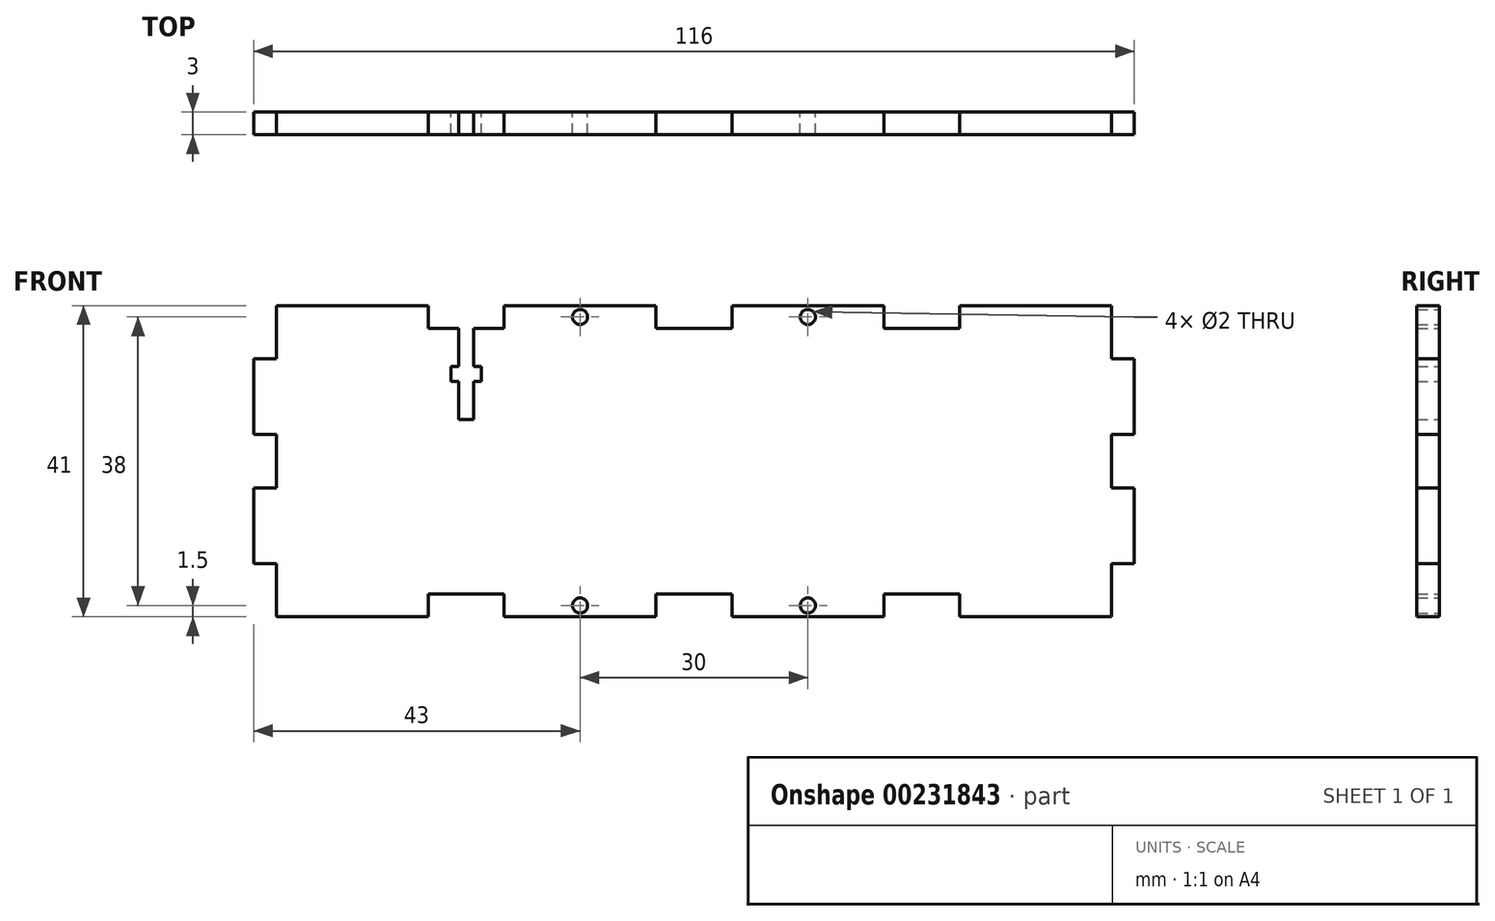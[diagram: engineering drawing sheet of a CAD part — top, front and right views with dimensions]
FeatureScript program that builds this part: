
annotation { "Feature Type Name" : "Feature", "Feature Type Description" : "" }
export const myFeature = defineFeature(function(context is Context, id is Id, definition is map)
    precondition{}
    {
        {
            var Q0;
            Q0=qCreatedBy(makeId("Front.planeOp"),FACE);
            var sketch = newSketch(context, id + "F0", { "sketchPlane" : qUnion([Q0])});
            skLineSegment(sketch, "E0", {"start": v(0, 0) * mm, "end": v(0, 7) * mm});
            skLineSegment(sketch, "E1", {"start": v(0, 7) * mm, "end": v(3, 7) * mm});
            skLineSegment(sketch, "E2", {"start": v(3, 7) * mm, "end": v(3, 17) * mm});
            skLineSegment(sketch, "E3", {"start": v(3, 17) * mm, "end": v(0, 17) * mm});
            skLineSegment(sketch, "E4", {"start": v(0, 17) * mm, "end": v(0, 24) * mm});
            skLineSegment(sketch, "E5", {"start": v(0, 24) * mm, "end": v(3, 24) * mm});
            skLineSegment(sketch, "E6", {"start": v(3, 24) * mm, "end": v(3, 34) * mm});
            skLineSegment(sketch, "E7", {"start": v(3, 34) * mm, "end": v(0, 34) * mm});
            skLineSegment(sketch, "E8", {"start": v(0, 34) * mm, "end": v(0, 41) * mm});
            skLineSegment(sketch, "E9", {"start": v(0, 41) * mm, "end": v(-20, 41) * mm});
            skLineSegment(sketch, "E10", {"start": v(-20, 41) * mm, "end": v(-20, 38) * mm});
            skLineSegment(sketch, "E11", {"start": v(-20, 38) * mm, "end": v(-30, 38) * mm});
            skLineSegment(sketch, "E12", {"start": v(-30, 38) * mm, "end": v(-30, 41) * mm});
            skLineSegment(sketch, "E13", {"start": v(-30, 41) * mm, "end": v(-50, 41) * mm});
            skLineSegment(sketch, "E14", {"start": v(-50, 41) * mm, "end": v(-50, 38) * mm});
            skLineSegment(sketch, "E15", {"start": v(-50, 38) * mm, "end": v(-60, 38) * mm});
            skLineSegment(sketch, "E16", {"start": v(-60, 38) * mm, "end": v(-60, 41) * mm});
            skLineSegment(sketch, "E17", {"start": v(-60, 41) * mm, "end": v(-80, 41) * mm});
            skLineSegment(sketch, "E18", {"start": v(-80, 41) * mm, "end": v(-80, 38) * mm});
            skLineSegment(sketch, "E19", {"start": v(-80, 38) * mm, "end": v(-84, 38) * mm});
            skLineSegment(sketch, "E20", {"start": v(-90, 38) * mm, "end": v(-90, 41) * mm});
            skLineSegment(sketch, "E21", {"start": v(-90, 41) * mm, "end": v(-110, 41) * mm});
            skLineSegment(sketch, "E22", {"start": v(0, 20.5) * mm, "end": v(-120, 20.5) * mm, "construction": true});
            skLineSegment(sketch, "E23.MirrorCS", {"start": v(-50, 0) * mm, "end": v(-50, 3) * mm});
            skLineSegment(sketch, "E24.MirrorCS", {"start": v(-60, 3) * mm, "end": v(-60, 0) * mm});
            skLineSegment(sketch, "E25.MirrorCS", {"start": v(-80, 0) * mm, "end": v(-80, 3) * mm});
            skLineSegment(sketch, "E26.MirrorCS", {"start": v(-90, 3) * mm, "end": v(-90, 0) * mm});
            skLineSegment(sketch, "E27.MirrorCS", {"start": v(-30, 3) * mm, "end": v(-30, 0) * mm});
            skLineSegment(sketch, "E28.MirrorCS", {"start": v(-20, 0) * mm, "end": v(-20, 3) * mm});
            skLineSegment(sketch, "E29.MirrorCS", {"start": v(-50, 3) * mm, "end": v(-60, 3) * mm});
            skLineSegment(sketch, "E30.MirrorCS", {"start": v(-60, 0) * mm, "end": v(-80, 0) * mm});
            skLineSegment(sketch, "E31.MirrorCS", {"start": v(-30, 0) * mm, "end": v(-50, 0) * mm});
            skLineSegment(sketch, "E32.MirrorCS", {"start": v(-80, 3) * mm, "end": v(-90, 3) * mm});
            skLineSegment(sketch, "E33.MirrorCS", {"start": v(-90, 0) * mm, "end": v(-110, 0) * mm});
            skLineSegment(sketch, "E34.MirrorCS", {"start": v(0, 0) * mm, "end": v(-20, 0) * mm});
            skLineSegment(sketch, "E35.MirrorCS", {"start": v(-20, 3) * mm, "end": v(-30, 3) * mm});
            skLineSegment(sketch, "E36", {"start": v(-55, 38) * mm, "end": v(-55, -6.16) * mm, "construction": true});
            skPoint(sketch, "E36.endSnap0", {"position": v(-55, 3) * mm});
            skLineSegment(sketch, "E37.MirrorCS", {"start": v(-113, 17) * mm, "end": v(-110, 17) * mm});
            skLineSegment(sketch, "E38.MirrorCS", {"start": v(-110, 24) * mm, "end": v(-113, 24) * mm});
            skLineSegment(sketch, "E39.MirrorCS", {"start": v(-113, 34) * mm, "end": v(-110, 34) * mm});
            skLineSegment(sketch, "E40.MirrorCS", {"start": v(-110, 7) * mm, "end": v(-113, 7) * mm});
            skLineSegment(sketch, "E41.MirrorCS", {"start": v(-110, 17) * mm, "end": v(-110, 24) * mm});
            skLineSegment(sketch, "E42.MirrorCS", {"start": v(-113, 7) * mm, "end": v(-113, 17) * mm});
            skLineSegment(sketch, "E43.MirrorCS", {"start": v(-113, 24) * mm, "end": v(-113, 34) * mm});
            skLineSegment(sketch, "E44.MirrorCS", {"start": v(-110, 34) * mm, "end": v(-110, 41) * mm});
            skLineSegment(sketch, "E45.MirrorCS", {"start": v(-110, 0) * mm, "end": v(-110, 7) * mm});
            skCircle(sketch, "E46", {"center": v(-40, 1.5) * mm, "radius": 1 * mm});
            skPoint(sketch, "E46.centerSnap0", {"position": v(-50, 1.5) * mm});
            skPoint(sketch, "E46.centerSnap1", {"position": v(-40, 0) * mm});
            skCircle(sketch, "E47.MirrorC", {"center": v(-70, 1.5) * mm, "radius": 1 * mm});
            skCircle(sketch, "E48.MirrorC", {"center": v(-70, 39.5) * mm, "radius": 1 * mm});
            skCircle(sketch, "E49.MirrorC", {"center": v(-40, 39.5) * mm, "radius": 1 * mm});
            skLineSegment(sketch, "E50", {"start": v(-85, 38) * mm, "end": v(-85, 18.99) * mm, "construction": true});
            skLineSegment(sketch, "E51.top", {"start": v(-86, 26) * mm, "end": v(-84, 26) * mm});
            skLineSegment(sketch, "E51.left", {"start": v(-86, 38) * mm, "end": v(-86, 33) * mm});
            skLineSegment(sketch, "E51.right", {"start": v(-84, 38) * mm, "end": v(-84, 33) * mm});
            skLineSegment(sketch, "E52.trimOffspring", {"start": v(-86, 38) * mm, "end": v(-90, 38) * mm});
            skLineSegment(sketch, "E53.bottom", {"start": v(-87, 33) * mm, "end": v(-86, 33) * mm});
            skLineSegment(sketch, "E53.top", {"start": v(-87, 31) * mm, "end": v(-86, 31) * mm});
            skLineSegment(sketch, "E53.left", {"start": v(-87, 33) * mm, "end": v(-87, 31) * mm});
            skLineSegment(sketch, "E53.right", {"start": v(-83, 33) * mm, "end": v(-83, 31) * mm});
            skLineSegment(sketch, "E54.trimOffspring", {"start": v(-84, 33) * mm, "end": v(-83, 33) * mm});
            skLineSegment(sketch, "E55.trimOffspring", {"start": v(-84, 31) * mm, "end": v(-84, 26) * mm});
            skLineSegment(sketch, "E56.trimOffspring", {"start": v(-86, 31) * mm, "end": v(-86, 26) * mm});
            skLineSegment(sketch, "E57.trimOffspring", {"start": v(-84, 31) * mm, "end": v(-83, 31) * mm});
            skSolve(sketch);
        }
        {
            var Q0;
            Q0 = qSketchRegion(id + "F0", true);
            extrude(context, id + "F1", {"entities" : qUnion([Q0]), "endBound" : BoundingType.SYMMETRIC, "depth" : 3 * mm});
        }
    });
